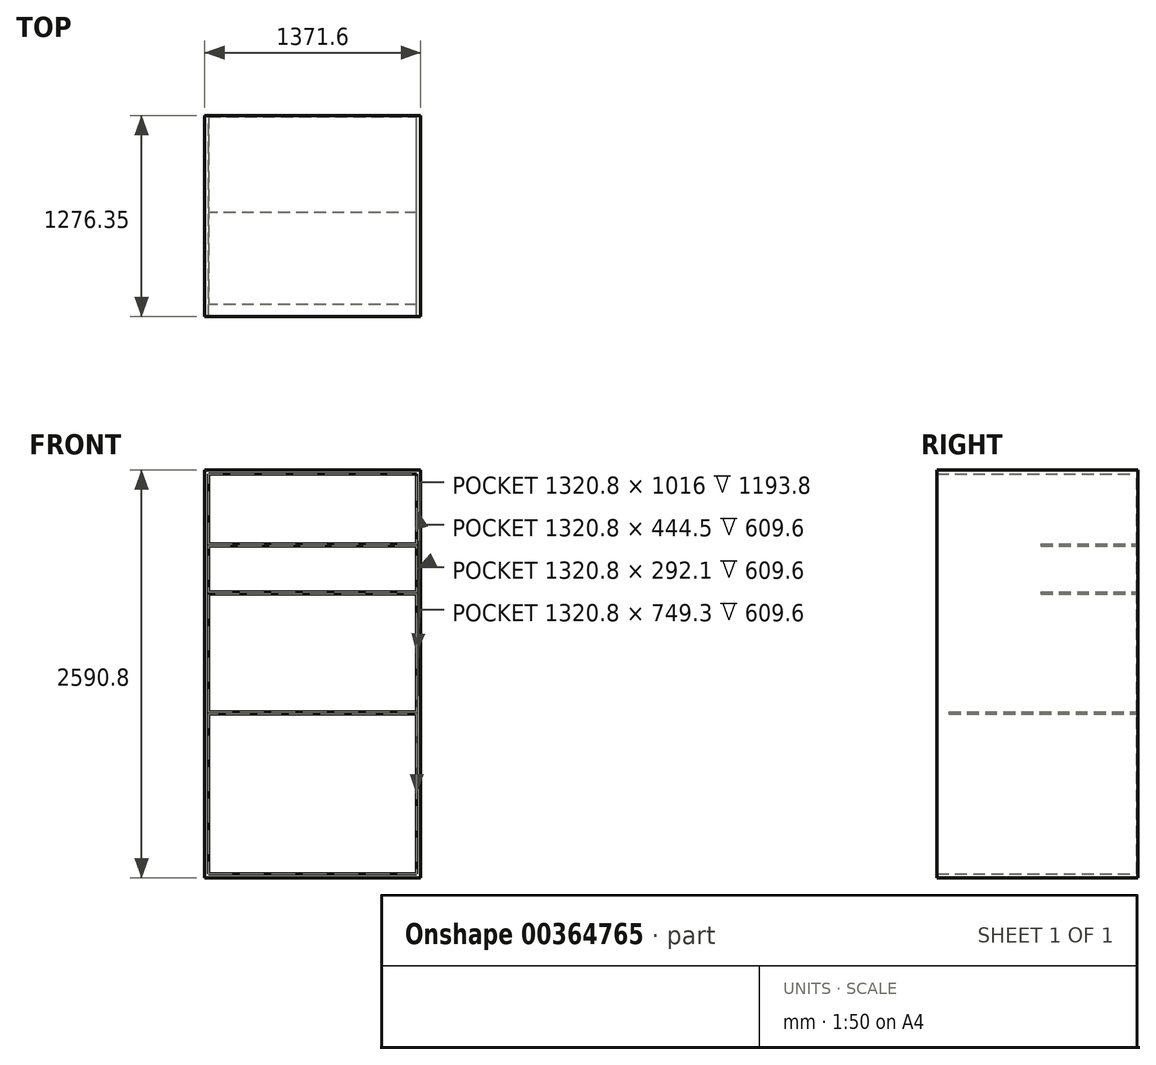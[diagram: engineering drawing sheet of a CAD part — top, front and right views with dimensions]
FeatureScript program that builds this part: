
annotation { "Feature Type Name" : "Feature", "Feature Type Description" : "" }
export const myFeature = defineFeature(function(context is Context, id is Id, definition is map)
    precondition{}
    {
        {
            var Q0;
            Q0=qCreatedBy(makeId("Front.planeOp"),FACE);
            var sketch = newSketch(context, id + "F0", { "sketchPlane" : qUnion([Q0])});
            skLineSegment(sketch, "E0.bottom", {"start": v(0, 0) * mm, "end": v(1320.8, 0) * mm});
            skLineSegment(sketch, "E0.top", {"start": v(0, 2540) * mm, "end": v(1320.8, 2540) * mm});
            skLineSegment(sketch, "E0.left", {"start": v(0, 0) * mm, "end": v(0, 2540) * mm});
            skLineSegment(sketch, "E0.right", {"start": v(1320.8, 0) * mm, "end": v(1320.8, 2540) * mm});
            skLineSegment(sketch, "E1.0", {"start": v(-25.4, -25.4) * mm, "end": v(-25.4, 2565.4) * mm});
            skLineSegment(sketch, "E1.1", {"start": v(-25.4, -25.4) * mm, "end": v(1346.2, -25.4) * mm});
            skLineSegment(sketch, "E1.2", {"start": v(1346.2, -25.4) * mm, "end": v(1346.2, 2565.4) * mm});
            skLineSegment(sketch, "E1.3", {"start": v(-25.4, 2565.4) * mm, "end": v(1346.2, 2565.4) * mm});
            skSolve(sketch);
        }
        {
            var Q0;
            Q0 = qSketchRegion(id + "F0", true);
            extrude(context, id + "F1", {"entities" : qUnion([Q0]), "depth" : 1270 * mm});
        }
        {
            var Q0;
            Q0=makeQuery(id+"F1.opExtrude","SWEPT_FACE",FACE,{"disambiguationData":[OSD([sQuery(id+"F0.wireOp",EDGE,"E0.left")])]});
            var sketch = newSketch(context, id + "F2", { "sketchPlane" : qUnion([Q0])});
            skLineSegment(sketch, "E2.bottom", {"start": v(0, 1016) * mm, "end": v(-1193.8, 1016) * mm});
            skLineSegment(sketch, "E2.top", {"start": v(0, 1028.7) * mm, "end": v(-1193.8, 1028.7) * mm});
            skLineSegment(sketch, "E2.left", {"start": v(0, 1016) * mm, "end": v(0, 1028.7) * mm});
            skLineSegment(sketch, "E2.right", {"start": v(-1193.8, 1016) * mm, "end": v(-1193.8, 1028.7) * mm});
            skPoint(sketch, "E3.oppositeSnap0", {"position": v(-596.9, 1028.7) * mm});
            skLineSegment(sketch, "E4.bottom", {"start": v(0, 2082.8) * mm, "end": v(-609.6, 2082.8) * mm});
            skLineSegment(sketch, "E4.top", {"start": v(0, 2095.5) * mm, "end": v(-609.6, 2095.5) * mm});
            skLineSegment(sketch, "E4.left", {"start": v(0, 2082.8) * mm, "end": v(0, 2095.5) * mm});
            skLineSegment(sketch, "E4.right", {"start": v(-609.6, 2082.8) * mm, "end": v(-609.6, 2095.5) * mm});
            skLineSegment(sketch, "E5.bottom", {"start": v(0, 1778) * mm, "end": v(-609.6, 1778) * mm});
            skLineSegment(sketch, "E5.top", {"start": v(0, 1790.7) * mm, "end": v(-609.6, 1790.7) * mm});
            skLineSegment(sketch, "E5.left", {"start": v(0, 1778) * mm, "end": v(0, 1790.7) * mm});
            skLineSegment(sketch, "E5.right", {"start": v(-609.6, 1778) * mm, "end": v(-609.6, 1790.7) * mm});
            skSolve(sketch);
        }
        {
            var Q0;
            Q0 = qSketchRegion(id + "F2", true);
            var Q1;
            Q1=makeQuery(id+"F1.opExtrude","SWEPT_FACE",FACE,{"disambiguationData":[OSD([sQuery(id+"F0.wireOp",EDGE,"E0.right")])]});
            extrude(context, id + "F3", {"entities" : qUnion([Q0]), "operationType" : NewBodyOperationType.ADD, "endBound" : BoundingType.UP_TO_SURFACE, "endBoundEntityFace" : qUnion([Q1]), "depth" : 25.4 * mm});
        }
        {
            var Q0;
            Q0=makeQuery(id+"F3.boolean.opBoolean","MERGE",FACE,{"derivedFrom":[makeQuery(id+"F1.opExtrude","CAP_FACE",FACE,{"disambiguationData":[OSD([sQuery(id+"F0.wireOp",EDGE,"E0.bottom"),sQuery(id+"F0.wireOp",EDGE,"E0.top"),sQuery(id+"F0.wireOp",EDGE,"E0.left"),sQuery(id+"F0.wireOp",EDGE,"E0.right"),sQuery(id+"F0.wireOp",EDGE,"E1.0"),sQuery(id+"F0.wireOp",EDGE,"E1.1"),sQuery(id+"F0.wireOp",EDGE,"E1.2"),sQuery(id+"F0.wireOp",EDGE,"E1.3")])],"isStart":true}),makeQuery(id+"F3.opExtrude","SWEPT_FACE",FACE,{"disambiguationData":[OSD([sQuery(id+"F2.wireOp",EDGE,"E2.left")])]}),makeQuery(id+"F3.opExtrude","SWEPT_FACE",FACE,{"disambiguationData":[OSD([sQuery(id+"F2.wireOp",EDGE,"E4.left")])]}),makeQuery(id+"F3.opExtrude","SWEPT_FACE",FACE,{"disambiguationData":[OSD([sQuery(id+"F2.wireOp",EDGE,"E5.left")])]})]});
            var sketch = newSketch(context, id + "F4", { "sketchPlane" : qUnion([Q0])});
            skLineSegment(sketch, "E6.bottom", {"start": v(-1346.2, 2565.4) * mm, "end": v(25.4, 2565.4) * mm});
            skLineSegment(sketch, "E6.top", {"start": v(-1346.2, -25.4) * mm, "end": v(25.4, -25.4) * mm});
            skLineSegment(sketch, "E6.left", {"start": v(-1346.2, 2565.4) * mm, "end": v(-1346.2, -25.4) * mm});
            skLineSegment(sketch, "E6.right", {"start": v(25.4, 2565.4) * mm, "end": v(25.4, -25.4) * mm});
            skSolve(sketch);
        }
        {
            var Q0;
            Q0 = qSketchRegion(id + "F4", true);
            extrude(context, id + "F5", {"entities" : qUnion([Q0]), "operationType" : NewBodyOperationType.ADD, "depth" : 6.35 * mm});
        }
    });
